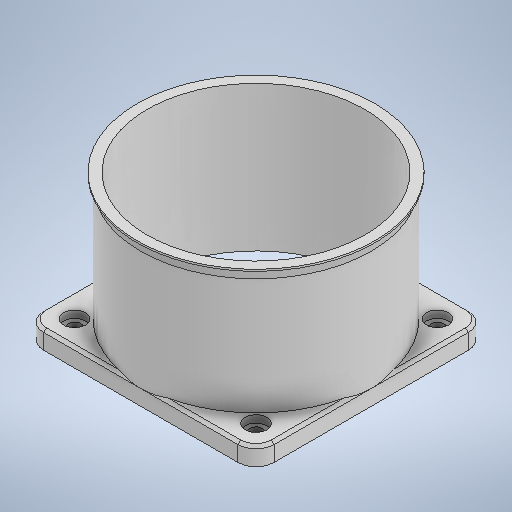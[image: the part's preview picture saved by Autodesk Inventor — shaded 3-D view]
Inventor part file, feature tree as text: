
AUTODESK INVENTOR PART (.ipt)
format: ipt  version: 2025.1 (Build 291241000, 241)  size: 312,320 bytes
history: native  units: in
note: dims shown in document units (in); Inventor stores cm internally (conversion verified against a paired STEP export)
features: sketch x5, extrude x3, chamfer x2, sweep x1
ambient origin geometry x8: Origin, YZ Plane, XZ Plane, XY Plane, X Axis, Y Axis, Z Axis, Center Point
bodies: Solid1 (feature_tree)
feature tree (11):
  extrude  "Extrusion1"  Depth=2.3622in
  extrude  "Extrusion2"  Depth=1.9685in
  sweep  "Sweep1"
  extrude  "Extrusion3"  Depth=0.1969in
  chamfer  "Chamfer1"  Distance=2.5in
  chamfer  "Chamfer2"  Distance=0.1969in
  sketch  "Sketch1"  dims[d1=0.1378in d2=2.3622in]
  sketch  "Sketch2"  dims[d3=1.9685in d4=1.9685in]
  sketch  "Sketch3"  dims[d5=0.9843in d6=0.9843in]
  sketch  "Sketch4"  dims[d7=0.1969in d8=0.1969in]
  sketch  "Sketch5"  dims[d9=2.5in d10=2.5in d11=0.1969in d12=0.0in d13=0.2362in d14=0.0787in d15=0.0in d16=180.0deg d17=1.1811in d18=0.9843in d19=0.3937in d20=0.0in d21=0.0in d22=0.0394in d23=0.1181in d24=0.0in d25=0.0394in d26=0.0984in d27=45.0deg d28=0.0295in d29=0.0787in d30=45.0deg]
